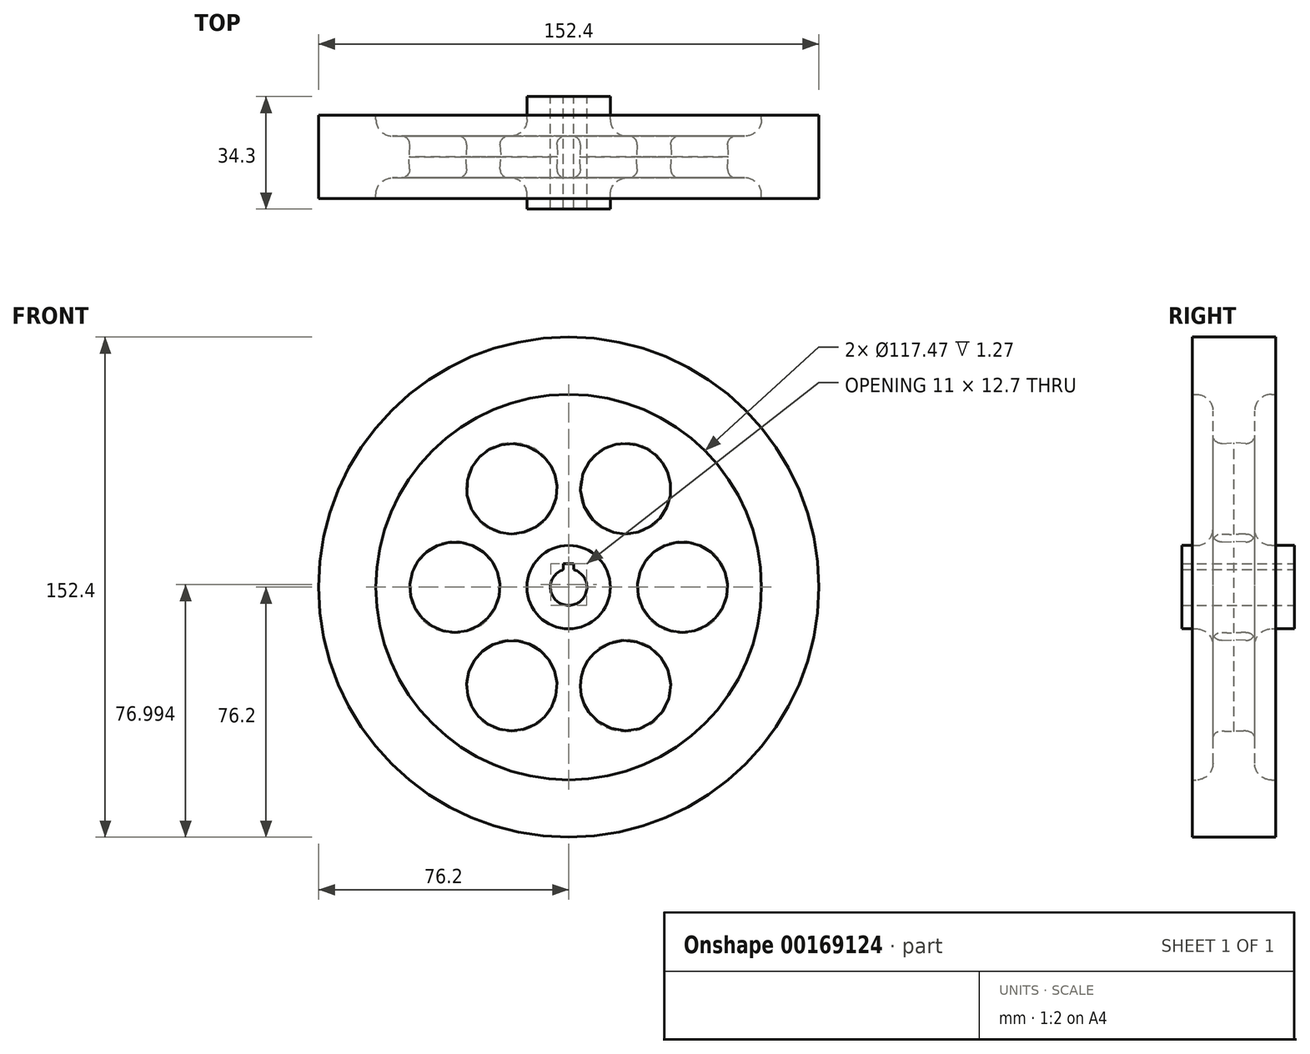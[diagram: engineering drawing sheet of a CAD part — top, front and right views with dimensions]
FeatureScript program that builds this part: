
annotation { "Feature Type Name" : "Feature", "Feature Type Description" : "" }
export const myFeature = defineFeature(function(context is Context, id is Id, definition is map)
    precondition{}
    {
        {
            var Q0;
            Q0=qCreatedBy(makeId("Front.planeOp"),FACE);
            var sketch = newSketch(context, id + "F0", { "sketchPlane" : qUnion([Q0])});
            skCircle(sketch, "E0", {"center": v(0, 0) * mm, "radius": 76.2 * mm});
            skCircle(sketch, "E1", {"center": v(0, 0) * mm, "radius": 58.74 * mm});
            skCircle(sketch, "E2", {"center": v(0, 0) * mm, "radius": 12.7 * mm});
            skArc(sketch, "E3", {"start": v(-1.59, 5.32) * mm, "mid": v(0, -5.56) * mm, "end": v(1.59, 5.32) * mm});
            skLineSegment(sketch, "E4.bottom", {"start": v(-1.59, 7.14) * mm, "end": v(1.59, 7.14) * mm});
            skLineSegment(sketch, "E4.left", {"start": v(-1.59, 7.14) * mm, "end": v(-1.59, 5.32) * mm});
            skLineSegment(sketch, "E4.right", {"start": v(1.59, 7.14) * mm, "end": v(1.59, 5.32) * mm});
            skSolve(sketch);
        }
        {
            var Q0;
            Q0=makeQuery(id+"F0.imprint","IMPRINT",FACE,{"disambiguationData":[TD([[makeQuery(id+"F0.imprint","IMPRINT",EDGE,{"derivedFrom":sQuery(id+"F0.wireOp",EDGE,"E0")}),1.0]])]});
            extrude(context, id + "F1", {"entities" : qUnion([Q0]), "depth" : 12.7 * mm, "hasSecondDirection" : true, "secondDirectionOppositeDirection" : true, "secondDirectionDepth" : 12.7 * mm});
        }
        {
            var Q0;
            Q0=makeQuery(id+"F0.imprint","IMPRINT",FACE,{"disambiguationData":[TD([[makeQuery(id+"F0.imprint","IMPRINT",EDGE,{"derivedFrom":sQuery(id+"F0.wireOp",EDGE,"E2")}),1.0]])]});
            extrude(context, id + "F2", {"entities" : qUnion([Q0]), "depth" : 15.88 * mm, "hasSecondDirection" : true, "secondDirectionOppositeDirection" : true, "secondDirectionDepth" : 18.41 * mm});
        }
        {
            var Q0;
            Q0=makeQuery(id+"F0.imprint","IMPRINT",FACE,{"disambiguationData":[TD([[makeQuery(id+"F0.imprint","IMPRINT",EDGE,{"derivedFrom":sQuery(id+"F0.wireOp",EDGE,"E1")}),1.0]])]});
            var sketch = newSketch(context, id + "F3", { "sketchPlane" : qUnion([Q0])});
            skCircle(sketch, "E5", {"center": v(0, 0) * mm, "radius": 9.49 * mm});
            skCircle(sketch, "E6", {"center": v(0, 0) * mm, "radius": 62.67 * mm});
            skCircle(sketch, "E7", {"center": v(-34.66, 0) * mm, "radius": 13.97 * mm});
            skCircle(sketch, "E8.1.0", {"center": v(-17.33, -30.01) * mm, "radius": 13.97 * mm});
            skCircle(sketch, "E8.2.0", {"center": v(17.33, -30.01) * mm, "radius": 13.97 * mm});
            skCircle(sketch, "E8.3.0", {"center": v(34.66, 0) * mm, "radius": 13.97 * mm});
            skCircle(sketch, "E8.4.0", {"center": v(17.33, 30.01) * mm, "radius": 13.97 * mm});
            skCircle(sketch, "E8.5.0", {"center": v(-17.33, 30.01) * mm, "radius": 13.97 * mm});
            skSolve(sketch);
        }
        {
            var Q0;
            Q0 = qSketchRegion(id + "F3", true);
            extrude(context, id + "F4", {"entities" : qUnion([Q0]), "depth" : 6.35 * mm, "hasDraft" : true, "draftAngle" : 3 * degree, "hasSecondDirection" : true, "secondDirectionOppositeDirection" : true, "secondDirectionDepth" : 6.35 * mm, "hasSecondDirectionDraft" : true, "secondDirectionDraftAngle" : 3 * degree});
        }
        {
            var Q0;
            Q0=makeQuery(id+"F2.opExtrude","SWEPT_BODY",BODY,{"disambiguationData":[OSD([sQuery(id+"F0.wireOp",EDGE,"E2"),sQuery(id+"F0.wireOp",EDGE,"E3"),sQuery(id+"F0.wireOp",EDGE,"E4.bottom"),sQuery(id+"F0.wireOp",EDGE,"E4.left"),sQuery(id+"F0.wireOp",EDGE,"E4.right")])]});
            var Q1;
            Q1=makeQuery(id+"F4.split0.splitOp","SPLIT",BODY,{"derivedFrom":makeQuery(id+"F4.opExtrude","SWEPT_BODY",BODY,{"disambiguationData":[OSD([sQuery(id+"F3.wireOp",EDGE,"E5"),sQuery(id+"F3.wireOp",EDGE,"E6"),sQuery(id+"F3.wireOp",EDGE,"E7"),sQuery(id+"F3.wireOp",EDGE,"E8.1.0"),sQuery(id+"F3.wireOp",EDGE,"E8.2.0"),sQuery(id+"F3.wireOp",EDGE,"E8.3.0"),sQuery(id+"F3.wireOp",EDGE,"E8.4.0"),sQuery(id+"F3.wireOp",EDGE,"E8.5.0")])]})});
            var Q2;
            Q2=makeQuery(id+"F1.opExtrude","SWEPT_BODY",BODY,{"disambiguationData":[OSD([sQuery(id+"F0.wireOp",EDGE,"E0"),sQuery(id+"F0.wireOp",EDGE,"E1")])]});
            booleanBodies(context, id + "F5", {"operationType" : BooleanOperationType.UNION, "tools" : qUnion([Q0, Q1, Q2])});
        }
        {
            var Q0;
            Q0=makeQuery(id+"F5.opBoolean","INTERSECT",EDGE,{"derivedFrom":[makeQuery(id+"F2.opExtrude","SWEPT_FACE",FACE,{"disambiguationData":[OSD([sQuery(id+"F0.wireOp",EDGE,"E2")])]}),makeQuery(id+"F4.opExtrude","CAP_FACE",FACE,{"disambiguationData":[OSD([sQuery(id+"F3.wireOp",EDGE,"E5"),sQuery(id+"F3.wireOp",EDGE,"E6"),sQuery(id+"F3.wireOp",EDGE,"E7"),sQuery(id+"F3.wireOp",EDGE,"E8.1.0"),sQuery(id+"F3.wireOp",EDGE,"E8.2.0"),sQuery(id+"F3.wireOp",EDGE,"E8.3.0"),sQuery(id+"F3.wireOp",EDGE,"E8.4.0"),sQuery(id+"F3.wireOp",EDGE,"E8.5.0")])],"isStart":false})]});
            var Q1;
            Q1=makeQuery(id+"F5.opBoolean","INTERSECT",EDGE,{"derivedFrom":[makeQuery(id+"F1.opExtrude","SWEPT_FACE",FACE,{"disambiguationData":[OSD([sQuery(id+"F0.wireOp",EDGE,"E1")])]}),makeQuery(id+"F4.opExtrude","CAP_FACE",FACE,{"disambiguationData":[OSD([sQuery(id+"F3.wireOp",EDGE,"E5"),sQuery(id+"F3.wireOp",EDGE,"E6"),sQuery(id+"F3.wireOp",EDGE,"E7"),sQuery(id+"F3.wireOp",EDGE,"E8.1.0"),sQuery(id+"F3.wireOp",EDGE,"E8.2.0"),sQuery(id+"F3.wireOp",EDGE,"E8.3.0"),sQuery(id+"F3.wireOp",EDGE,"E8.4.0"),sQuery(id+"F3.wireOp",EDGE,"E8.5.0")])],"isStart":false})]});
            var Q2;
            Q2=makeQuery(id+"F5.opBoolean","INTERSECT",EDGE,{"derivedFrom":[makeQuery(id+"F1.opExtrude","SWEPT_FACE",FACE,{"disambiguationData":[OSD([sQuery(id+"F0.wireOp",EDGE,"E1")])]}),makeQuery(id+"F4.opExtrude","CAP_FACE",FACE,{"disambiguationData":[OSD([sQuery(id+"F3.wireOp",EDGE,"E5"),sQuery(id+"F3.wireOp",EDGE,"E6"),sQuery(id+"F3.wireOp",EDGE,"E7"),sQuery(id+"F3.wireOp",EDGE,"E8.1.0"),sQuery(id+"F3.wireOp",EDGE,"E8.2.0"),sQuery(id+"F3.wireOp",EDGE,"E8.3.0"),sQuery(id+"F3.wireOp",EDGE,"E8.4.0"),sQuery(id+"F3.wireOp",EDGE,"E8.5.0")])],"isStart":true})]});
            var Q3;
            Q3=makeQuery(id+"F5.opBoolean","INTERSECT",EDGE,{"derivedFrom":[makeQuery(id+"F2.opExtrude","SWEPT_FACE",FACE,{"disambiguationData":[OSD([sQuery(id+"F0.wireOp",EDGE,"E2")])]}),makeQuery(id+"F4.opExtrude","CAP_FACE",FACE,{"disambiguationData":[OSD([sQuery(id+"F3.wireOp",EDGE,"E5"),sQuery(id+"F3.wireOp",EDGE,"E6"),sQuery(id+"F3.wireOp",EDGE,"E7"),sQuery(id+"F3.wireOp",EDGE,"E8.1.0"),sQuery(id+"F3.wireOp",EDGE,"E8.2.0"),sQuery(id+"F3.wireOp",EDGE,"E8.3.0"),sQuery(id+"F3.wireOp",EDGE,"E8.4.0"),sQuery(id+"F3.wireOp",EDGE,"E8.5.0")])],"isStart":true})]});
            fillet(context, id + "F6", {"entities" : qUnion([Q0, Q1, Q2, Q3]), "radius" : 5.08 * mm, "tangentPropagation" : true, "allowEdgeOverflow" : false});
        }
        {
            var Q0;
            Q0=makeQuery(id+"F4.opExtrude","CAP_EDGE",EDGE,{"disambiguationData":[OSD([sQuery(id+"F3.wireOp",EDGE,"E8.2.0")])],"isStart":true});
            var Q1;
            Q1=makeQuery(id+"F4.opExtrude","CAP_EDGE",EDGE,{"disambiguationData":[OSD([sQuery(id+"F3.wireOp",EDGE,"E8.3.0")])],"isStart":true});
            var Q2;
            Q2=makeQuery(id+"F4.opExtrude","CAP_EDGE",EDGE,{"disambiguationData":[OSD([sQuery(id+"F3.wireOp",EDGE,"E8.4.0")])],"isStart":true});
            var Q3;
            Q3=makeQuery(id+"F4.opExtrude","CAP_EDGE",EDGE,{"disambiguationData":[OSD([sQuery(id+"F3.wireOp",EDGE,"E8.5.0")])],"isStart":true});
            var Q4;
            Q4=makeQuery(id+"F4.opExtrude","CAP_EDGE",EDGE,{"disambiguationData":[OSD([sQuery(id+"F3.wireOp",EDGE,"E7")])],"isStart":true});
            var Q5;
            Q5=makeQuery(id+"F4.opExtrude","CAP_EDGE",EDGE,{"disambiguationData":[OSD([sQuery(id+"F3.wireOp",EDGE,"E8.1.0")])],"isStart":true});
            var Q6;
            Q6=makeQuery(id+"F4.opExtrude","CAP_EDGE",EDGE,{"disambiguationData":[OSD([sQuery(id+"F3.wireOp",EDGE,"E7")])],"isStart":false});
            var Q7;
            Q7=makeQuery(id+"F4.opExtrude","CAP_EDGE",EDGE,{"disambiguationData":[OSD([sQuery(id+"F3.wireOp",EDGE,"E8.5.0")])],"isStart":false});
            var Q8;
            Q8=makeQuery(id+"F4.opExtrude","CAP_EDGE",EDGE,{"disambiguationData":[OSD([sQuery(id+"F3.wireOp",EDGE,"E8.4.0")])],"isStart":false});
            var Q9;
            Q9=makeQuery(id+"F4.opExtrude","CAP_EDGE",EDGE,{"disambiguationData":[OSD([sQuery(id+"F3.wireOp",EDGE,"E8.3.0")])],"isStart":false});
            var Q10;
            Q10=makeQuery(id+"F4.opExtrude","CAP_EDGE",EDGE,{"disambiguationData":[OSD([sQuery(id+"F3.wireOp",EDGE,"E8.2.0")])],"isStart":false});
            var Q11;
            Q11=makeQuery(id+"F4.opExtrude","CAP_EDGE",EDGE,{"disambiguationData":[OSD([sQuery(id+"F3.wireOp",EDGE,"E8.1.0")])],"isStart":false});
            fillet(context, id + "F7", {"entities" : qUnion([Q0, Q1, Q2, Q3, Q4, Q5, Q6, Q7, Q8, Q9, Q10, Q11]), "radius" : 2.54 * mm, "tangentPropagation" : true, "allowEdgeOverflow" : false});
        }
    });
